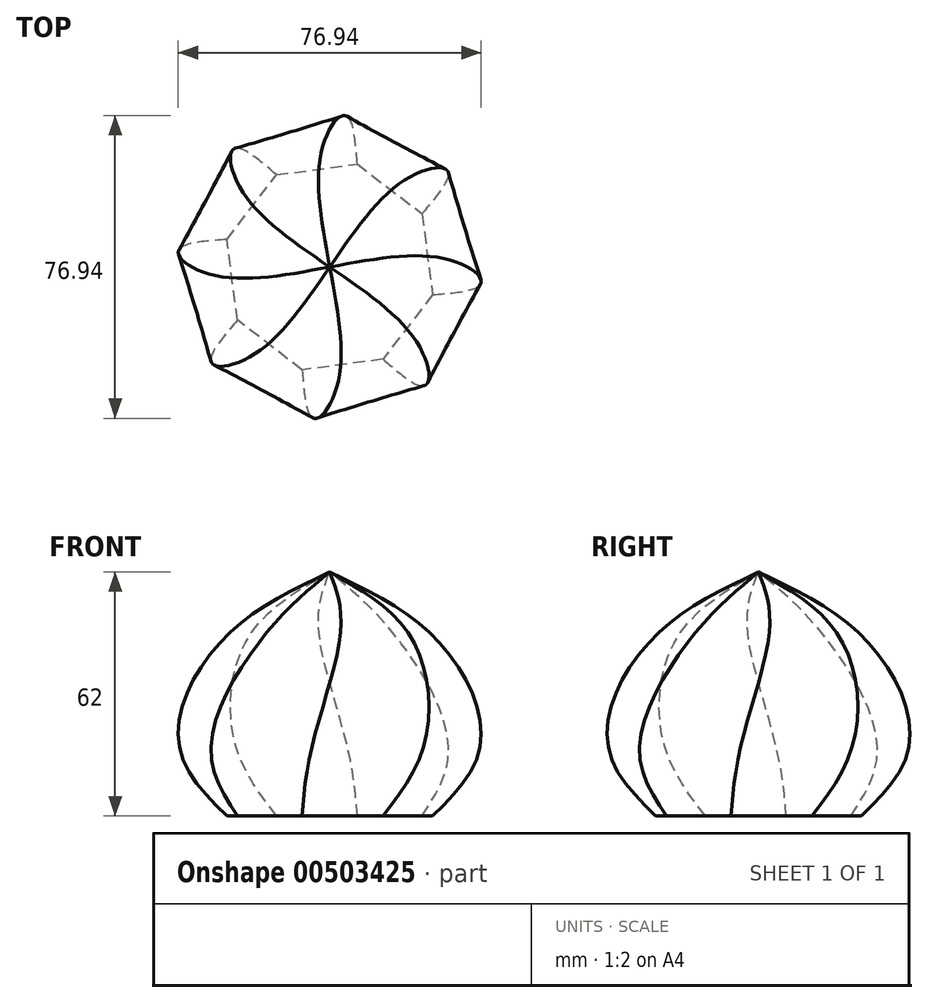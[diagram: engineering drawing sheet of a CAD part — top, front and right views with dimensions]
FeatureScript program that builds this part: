
annotation { "Feature Type Name" : "Feature", "Feature Type Description" : "" }
export const myFeature = defineFeature(function(context is Context, id is Id, definition is map)
    precondition{}
    {
        {
            var Q0;
            Q0=qCreatedBy(makeId("Top.planeOp"),FACE);
            cPlane(context, id + "F0", {"entities" : qUnion([Q0]), "cplaneType" : CPlaneType.OFFSET, "offset" : 15 * mm, "width" : 150 * mm, "height" : 150 * mm});
        }
        {
            var Q0;
            Q0=qCreatedBy(id+"F0.planeOp",FACE);
            cPlane(context, id + "F1", {"entities" : qUnion([Q0]), "cplaneType" : CPlaneType.OFFSET, "offset" : 30 * mm, "width" : 150 * mm, "height" : 150 * mm});
        }
        {
            var Q0;
            Q0=qCreatedBy(makeId("Top.planeOp"),FACE);
            var sketch = newSketch(context, id + "F2", { "sketchPlane" : qUnion([Q0])});
            skCircle(sketch, "E0.cCircle", {"center": v(0, 0) * mm, "radius": 25 * mm, "construction": true});
            skLineSegment(sketch, "E0.0", {"start": v(26.13, -7.02) * mm, "end": v(13.52, -23.44) * mm});
            skLineSegment(sketch, "E0.1", {"start": v(13.52, -23.44) * mm, "end": v(-7.02, -26.13) * mm});
            skLineSegment(sketch, "E0.2", {"start": v(-7.02, -26.13) * mm, "end": v(-23.44, -13.52) * mm});
            skLineSegment(sketch, "E0.3", {"start": v(-23.44, -13.52) * mm, "end": v(-26.13, 7.02) * mm});
            skLineSegment(sketch, "E0.4", {"start": v(-26.13, 7.02) * mm, "end": v(-13.52, 23.44) * mm});
            skLineSegment(sketch, "E0.5", {"start": v(-13.52, 23.44) * mm, "end": v(7.02, 26.13) * mm});
            skLineSegment(sketch, "E0.6", {"start": v(7.02, 26.13) * mm, "end": v(23.44, 13.52) * mm});
            skLineSegment(sketch, "E0.7", {"start": v(23.44, 13.52) * mm, "end": v(26.13, -7.02) * mm});
            skPoint(sketch, "E0.0.midPoint", {"position": v(19.82, -15.23) * mm});
            skSolve(sketch);
        }
        {
            var Q0;
            Q0=qCreatedBy(id+"F0.planeOp",FACE);
            var sketch = newSketch(context, id + "F3", { "sketchPlane" : qUnion([Q0])});
            skCircle(sketch, "E1.cCircle", {"center": v(0, 0) * mm, "radius": 35 * mm, "construction": true});
            skLineSegment(sketch, "E1.0", {"start": v(37.54, -5.1) * mm, "end": v(22.94, -30.15) * mm});
            skLineSegment(sketch, "E1.1", {"start": v(22.94, -30.15) * mm, "end": v(-5.1, -37.54) * mm});
            skLineSegment(sketch, "E1.2", {"start": v(-5.1, -37.54) * mm, "end": v(-30.15, -22.94) * mm});
            skLineSegment(sketch, "E1.3", {"start": v(-30.15, -22.94) * mm, "end": v(-37.54, 5.1) * mm});
            skLineSegment(sketch, "E1.4", {"start": v(-37.54, 5.1) * mm, "end": v(-22.94, 30.15) * mm});
            skLineSegment(sketch, "E1.5", {"start": v(-22.94, 30.15) * mm, "end": v(5.1, 37.54) * mm});
            skLineSegment(sketch, "E1.6", {"start": v(5.1, 37.54) * mm, "end": v(30.15, 22.94) * mm});
            skLineSegment(sketch, "E1.7", {"start": v(30.15, 22.94) * mm, "end": v(37.54, -5.1) * mm});
            skPoint(sketch, "E1.0.midPoint", {"position": v(30.24, -17.62) * mm});
            skSolve(sketch);
        }
        {
            var Q0;
            Q0=qCreatedBy(id+"F1.planeOp",FACE);
            var sketch = newSketch(context, id + "F4", { "sketchPlane" : qUnion([Q0])});
            skCircle(sketch, "E2.cCircle", {"center": v(0, 0) * mm, "radius": 25 * mm, "construction": true});
            skLineSegment(sketch, "E2.0", {"start": v(2.55, -26.94) * mm, "end": v(-17.25, -20.85) * mm});
            skLineSegment(sketch, "E2.1", {"start": v(-17.25, -20.85) * mm, "end": v(-26.94, -2.55) * mm});
            skLineSegment(sketch, "E2.2", {"start": v(-26.94, -2.55) * mm, "end": v(-20.85, 17.25) * mm});
            skLineSegment(sketch, "E2.3", {"start": v(-20.85, 17.25) * mm, "end": v(-2.55, 26.94) * mm});
            skLineSegment(sketch, "E2.4", {"start": v(-2.55, 26.94) * mm, "end": v(17.25, 20.85) * mm});
            skLineSegment(sketch, "E2.5", {"start": v(17.25, 20.85) * mm, "end": v(26.94, 2.55) * mm});
            skLineSegment(sketch, "E2.6", {"start": v(26.94, 2.55) * mm, "end": v(20.85, -17.25) * mm});
            skLineSegment(sketch, "E2.7", {"start": v(20.85, -17.25) * mm, "end": v(2.55, -26.94) * mm});
            skPoint(sketch, "E2.0.midPoint", {"position": v(-7.35, -23.9) * mm});
            skSolve(sketch);
        }
        {
            var Q0;
            Q0=qCreatedBy(id+"F1.planeOp",FACE);
            cPlane(context, id + "F5", {"entities" : qUnion([Q0]), "cplaneType" : CPlaneType.OFFSET, "offset" : 17 * mm, "width" : 150 * mm, "height" : 150 * mm});
        }
        {
            var Q0;
            Q0=qCreatedBy(id+"F5.planeOp",FACE);
            var sketch = newSketch(context, id + "F6", { "sketchPlane" : qUnion([Q0])});
            skPoint(sketch, "E3", {"position": v(0, 0) * mm});
            skSolve(sketch);
        }
        {
            var Q0;
            Q0=makeQuery(id+"F2.imprint","IMPRINT",FACE,{"disambiguationData":[TD([[makeQuery(id+"F2.imprint","IMPRINT",EDGE,{"derivedFrom":sQuery(id+"F2.wireOp",EDGE,"E0.0")}),-1.0]])]});
            var Q1;
            Q1=makeQuery(id+"F3.imprint","IMPRINT",FACE,{"disambiguationData":[TD([[makeQuery(id+"F3.imprint","IMPRINT",EDGE,{"derivedFrom":sQuery(id+"F3.wireOp",EDGE,"E1.0")}),-1.0]])]});
            var Q2;
            Q2=makeQuery(id+"F4.imprint","IMPRINT",FACE,{"disambiguationData":[TD([[makeQuery(id+"F4.imprint","IMPRINT",EDGE,{"derivedFrom":sQuery(id+"F4.wireOp",EDGE,"E2.0")}),-1.0]])]});
            var Q3;
            Q3=sQuery(id+"F6.wireOp",VERTEX,"E3");
            loft(context, id + "F7", {"bodyType" : ToolBodyType.SURFACE, "wireProfilesArray" : [{ "wireProfileEntities" : qUnion([Q0]) }, { "wireProfileEntities" : qUnion([Q1]) }, { "wireProfileEntities" : qUnion([Q2]) }, { "wireProfileEntities" : qUnion([Q3]) }]});
        }
    });
